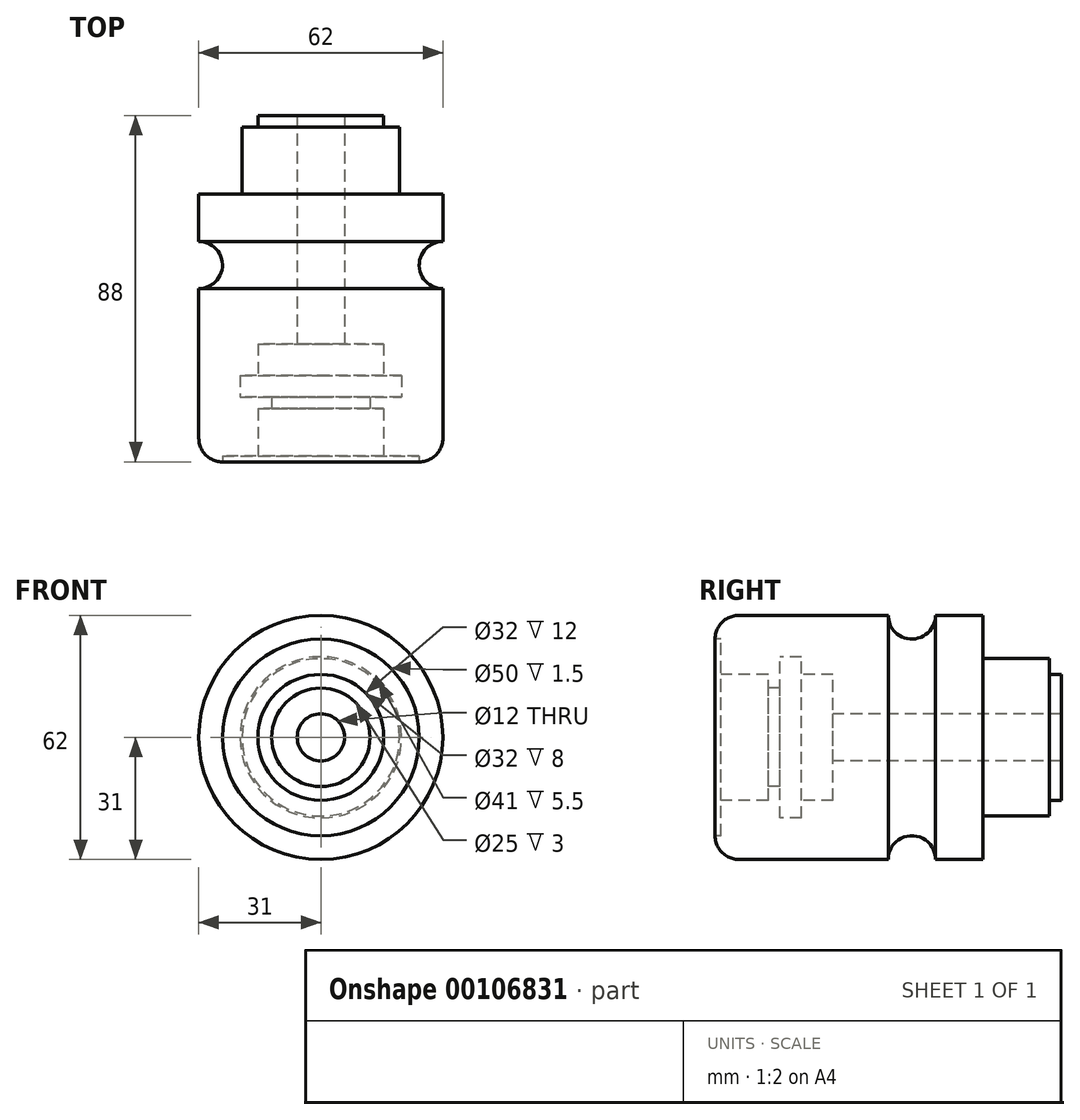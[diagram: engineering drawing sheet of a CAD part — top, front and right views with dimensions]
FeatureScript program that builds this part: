
annotation { "Feature Type Name" : "Feature", "Feature Type Description" : "" }
export const myFeature = defineFeature(function(context is Context, id is Id, definition is map)
    precondition{}
    {
        {
            var Q0;
            Q0=qCreatedBy(makeId("Right.planeOp"),FACE);
            var sketch = newSketch(context, id + "F0", { "sketchPlane" : qUnion([Q0])});
            skLineSegment(sketch, "E0", {"start": v(0, 0) * mm, "end": v(123.62, 0) * mm, "construction": true});
            skLineSegment(sketch, "E1", {"start": v(0, 0) * mm, "end": v(0, 25) * mm});
            skLineSegment(sketch, "E2", {"start": v(6, 31) * mm, "end": v(44, 31) * mm});
            skLineSegment(sketch, "E3", {"start": v(56, 31) * mm, "end": v(68, 31) * mm});
            skLineSegment(sketch, "E4", {"start": v(68, 31) * mm, "end": v(68, 20) * mm});
            skLineSegment(sketch, "E5", {"start": v(68, 20) * mm, "end": v(85, 20) * mm});
            skLineSegment(sketch, "E6", {"start": v(85, 20) * mm, "end": v(85, 16) * mm});
            skLineSegment(sketch, "E7", {"start": v(85, 16) * mm, "end": v(88, 16) * mm});
            skLineSegment(sketch, "E8", {"start": v(88, 16) * mm, "end": v(88, 0) * mm});
            skArc(sketch, "E9", {"start": v(44, 31) * mm, "mid": v(50, 25) * mm, "end": v(56, 31) * mm});
            skLineSegment(sketch, "E10", {"start": v(88, 0) * mm, "end": v(0, 0) * mm});
            skPoint(sketch, "E11.visualSharp", {"position": v(0, 31) * mm});
            skArc(sketch, "E11.filletArc", {"start": v(6, 31) * mm, "mid": v(1.76, 29.24) * mm, "end": v(0, 25) * mm});
            skSolve(sketch);
        }
        {
            var Q0;
            Q0=makeQuery(id+"F0.imprint","IMPRINT",FACE,{"disambiguationData":[TD([[makeQuery(id+"F0.imprint","IMPRINT",EDGE,{"derivedFrom":sQuery(id+"F0.wireOp",EDGE,"E1")}),-1.0]])]});
            var Q1;
            Q1=sQuery(id+"F0.wireOp",EDGE,"E0");
            revolve(context, id + "F1", {"entities" : qUnion([Q0]), "axis" : qUnion([Q1]), "revolveType" : RevolveType.FULL});
        }
        {
            var Q0;
            Q0=qCreatedBy(makeId("Right.planeOp"),FACE);
            var sketch = newSketch(context, id + "F2", { "sketchPlane" : qUnion([Q0])});
            skLineSegment(sketch, "E12", {"start": v(0, 0) * mm, "end": v(88, 0) * mm, "construction": true});
            skLineSegment(sketch, "E13", {"start": v(13.5, 16) * mm, "end": v(13.5, 12.5) * mm});
            skLineSegment(sketch, "E14", {"start": v(13.5, 12.5) * mm, "end": v(16.5, 12.5) * mm});
            skLineSegment(sketch, "E15", {"start": v(16.5, 12.5) * mm, "end": v(16.5, 20.5) * mm});
            skLineSegment(sketch, "E16", {"start": v(16.5, 20.5) * mm, "end": v(22, 20.5) * mm});
            skLineSegment(sketch, "E17", {"start": v(22, 20.5) * mm, "end": v(22, 16) * mm});
            skLineSegment(sketch, "E18", {"start": v(22, 16) * mm, "end": v(30, 16) * mm});
            skLineSegment(sketch, "E19", {"start": v(30, 6) * mm, "end": v(88, 6) * mm});
            skLineSegment(sketch, "E20", {"start": v(30, 16) * mm, "end": v(30, 6) * mm});
            skLineSegment(sketch, "E21", {"start": v(0, 0) * mm, "end": v(0, 25) * mm});
            skLineSegment(sketch, "E22", {"start": v(0, 25) * mm, "end": v(1.5, 25) * mm});
            skLineSegment(sketch, "E23", {"start": v(1.5, 25) * mm, "end": v(1.5, 0) * mm});
            skLineSegment(sketch, "E24", {"start": v(13.5, 16) * mm, "end": v(1.5, 16) * mm});
            skLineSegment(sketch, "E25", {"start": v(88, 6) * mm, "end": v(88, 0) * mm});
            skLineSegment(sketch, "E26", {"start": v(88, 0) * mm, "end": v(0, 0) * mm});
            skSolve(sketch);
        }
        {
            var Q0;
            Q0 = qSketchRegion(id + "F2", true);
            var Q1;
            Q1=sQuery(id+"F2.wireOp",EDGE,"E26");
            revolve(context, id + "F3", {"operationType" : NewBodyOperationType.REMOVE, "entities" : qUnion([Q0]), "axis" : qUnion([Q1]), "revolveType" : RevolveType.FULL, "oppositeDirection" : true});
        }
    });
